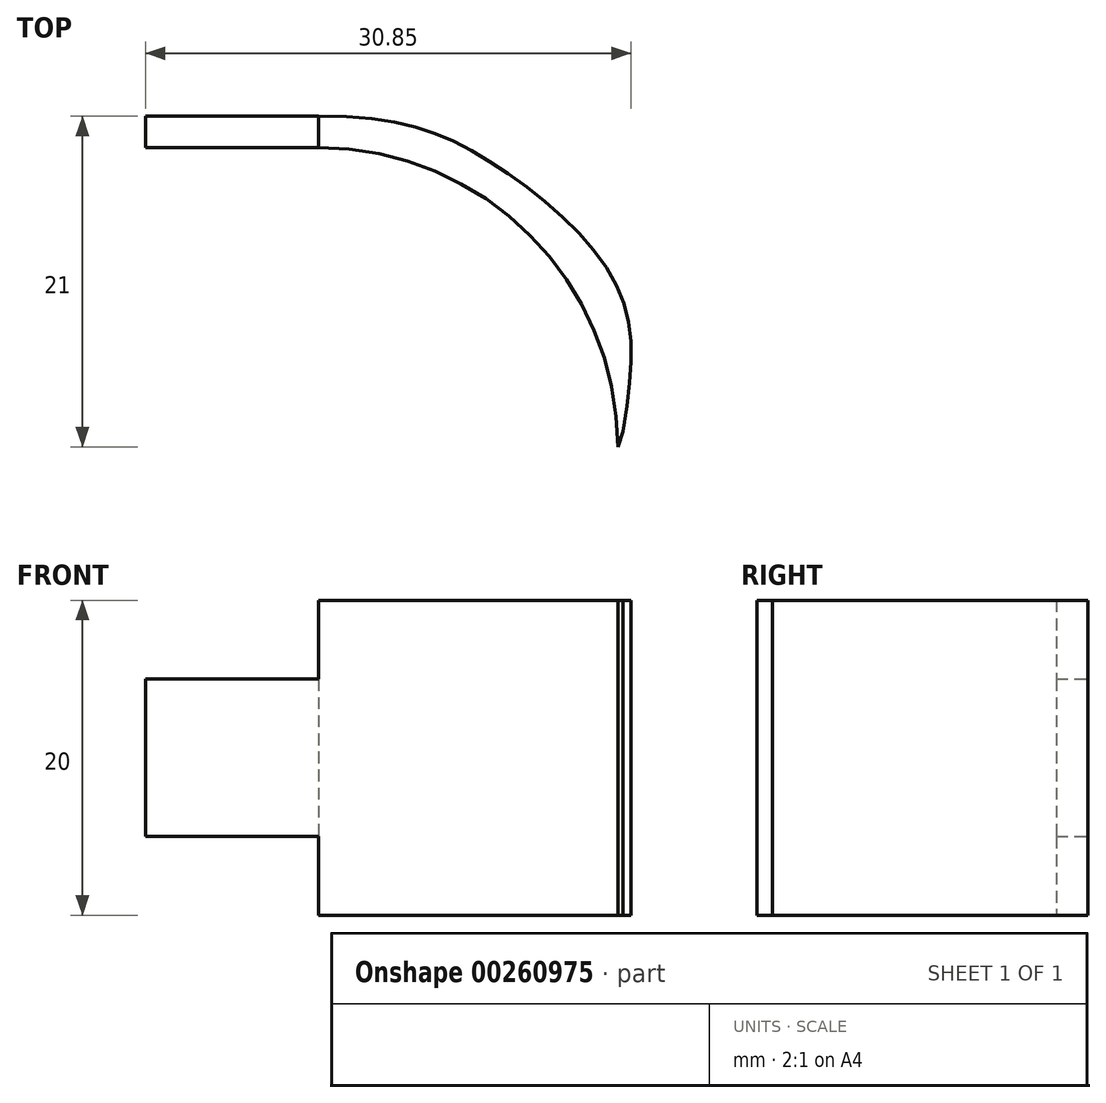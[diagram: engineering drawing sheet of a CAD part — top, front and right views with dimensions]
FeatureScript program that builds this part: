
annotation { "Feature Type Name" : "Feature", "Feature Type Description" : "" }
export const myFeature = defineFeature(function(context is Context, id is Id, definition is map)
    precondition{}
    {
        {
            var Q0;
            Q0=qCreatedBy(makeId("Top.planeOp"),FACE);
            var sketch = newSketch(context, id + "F0", { "sketchPlane" : qUnion([Q0])});
            skArc(sketch, "E0", {"start": v(19, 0) * mm, "mid": v(13.44, 13.44) * mm, "end": v(0, 19) * mm});
            skLineSegment(sketch, "E1", {"start": v(0, 21) * mm, "end": v(0, 19) * mm});
            skLineSegment(sketch, "E2", {"start": v(0, 19) * mm, "end": v(-11, 19) * mm});
            skLineSegment(sketch, "E3", {"start": v(-11, 19) * mm, "end": v(-11, 21) * mm});
            skLineSegment(sketch, "E4", {"start": v(-11, 21) * mm, "end": v(0, 21) * mm});
            skFitSpline(sketch, "E5", {"points": [v(0, 21) * mm, v(10.95, 18.08) * mm, v(19, 10.1) * mm, v(19, -1) * mm], "startDerivative": vector(45.21, 0.58) * mm, "endDerivative": vector(-7.44, -44.35) * mm});
            skLineSegment(sketch, "E6", {"start": v(19, 0) * mm, "end": v(19.33, 0.99) * mm});
            skPoint(sketch, "E7.orphan", {"position": v(0, 22) * mm});
            skLineSegment(sketch, "E8", {"start": v(19.82, 3.9) * mm, "end": v(19.33, 20.65) * mm, "construction": true});
            skSolve(sketch);
        }
        {
            var Q0;
            Q0=makeQuery(id+"F0.imprint","IMPRINT",FACE,{"disambiguationData":[TD([[makeQuery(id+"F0.imprint","IMPRINT",EDGE,{"derivedFrom":sQuery(id+"F0.wireOp",EDGE,"E0")}),-1.0]])]});
            var Q1;
            Q1=makeQuery(id+"F0.imprint","IMPRINT",FACE,{"disambiguationData":[TD([[makeQuery(id+"F0.imprint","IMPRINT",EDGE,{"derivedFrom":sQuery(id+"F0.wireOp",EDGE,"E1")}),-1.0]])]});
            extrude(context, id + "F1", {"entities" : qUnion([Q0, Q1]), "depth" : 20 * mm});
        }
        {
            var Q0;
            Q0=makeQuery(id+"F1.opExtrude","CAP_FACE",FACE,{"disambiguationData":[OSD([sQuery(id+"F0.wireOp",EDGE,"E0"),sQuery(id+"F0.wireOp",EDGE,"E2"),sQuery(id+"F0.wireOp",EDGE,"E3"),sQuery(id+"F0.wireOp",EDGE,"E4"),sQuery(id+"F0.wireOp",EDGE,"E5"),sQuery(id+"F0.wireOp",EDGE,"E6")])],"isStart":true});
            var sketch = newSketch(context, id + "F2", { "sketchPlane" : qUnion([Q0])});
            skLineSegment(sketch, "E9.0", {"start": v(-11, -21) * mm, "end": v(0, -21) * mm, "construction": true});
            skLineSegment(sketch, "E10", {"start": v(0, -21) * mm, "end": v(0, -19) * mm});
            skSolve(sketch);
        }
        {
            var Q0;
            Q0=makeQuery(id+"F2.imprint","IMPRINT",FACE,{"disambiguationData":[TD([[makeQuery(id+"F2.imprint","IMPRINT",EDGE,{"derivedFrom":sQuery(id+"F2.wireOp",EDGE,"E10")}),1.0]])]});
            extrude(context, id + "F3", {"entities" : qUnion([Q0]), "operationType" : NewBodyOperationType.REMOVE, "oppositeDirection" : true, "depth" : 5 * mm});
        }
        {
            var Q0;
            Q0=makeQuery(id+"F1.opExtrude","CAP_FACE",FACE,{"disambiguationData":[OSD([sQuery(id+"F0.wireOp",EDGE,"E0"),sQuery(id+"F0.wireOp",EDGE,"E2"),sQuery(id+"F0.wireOp",EDGE,"E3"),sQuery(id+"F0.wireOp",EDGE,"E4"),sQuery(id+"F0.wireOp",EDGE,"E5"),sQuery(id+"F0.wireOp",EDGE,"E6")])],"isStart":false});
            var sketch = newSketch(context, id + "F4", { "sketchPlane" : qUnion([Q0])});
            skLineSegment(sketch, "E11.0", {"start": v(-11, 21) * mm, "end": v(0, 21) * mm, "construction": true});
            skLineSegment(sketch, "E12", {"start": v(0, 21) * mm, "end": v(0, 19) * mm});
            skSolve(sketch);
        }
        {
            var Q0;
            Q0=makeQuery(id+"F4.imprint","IMPRINT",FACE,{"disambiguationData":[TD([[makeQuery(id+"F4.imprint","IMPRINT",EDGE,{"derivedFrom":sQuery(id+"F4.wireOp",EDGE,"E12")}),-1.0]])]});
            extrude(context, id + "F5", {"entities" : qUnion([Q0]), "operationType" : NewBodyOperationType.REMOVE, "oppositeDirection" : true, "depth" : 5 * mm});
        }
    });
